# Revit family: РОСМА_Термоманометр
name_source: partatom
category: Арматура трубопроводов
revit_build: Autodesk Revit 2018 (Build: 20180423_1000(x64)
units: mm (PartAtom-declared; Revit-internal decimal feet)

## family parameters
Всегда вертикально = Да
На основе рабочей плоскости = Нет
Общий = Нет
При загрузке вырезать с полостями = Нет
Размер круглого соединителя = Использовать диаметр
Тип детали = Вставляется

## types (4) — shared parameters
ADSK_Единица измерения = шт.
ADSK_Количество = 1
DN = 15.00 мм
Table = спец_термоманометр
Table_2 = размеры_термоманометр
URL = https://rosma.spb.ru
Группа модели = Оборудование
Диапазон раб. температур изм. среды = от 0°С до +100°С
Длина01 = ᅠ : 46мм
Длина02 = ᅠ : 64мм
Длина03 = ᅠ : 100мм
Изготовитель = ЗАО "РОСМА"
Класс точности = 2,5
Климатическое исполнение = Группа В3 по ГОСТ Р 52931; климатическое исполнение УХЛ категории 3.1 по ГОСТ 15150
Код IP = IP40
Межповерочный интервал = 2 года
Температура01 = ‎ : (0...+120°С)(0...0.25МПа)
Температура02 = ‎ : (0...+120°С)(0...0.4МПа)
Температура03 = ‎ : (0...+120°С)(0...0.6МПа)
Температура04 = ‎ : (0...+120°С)(0...1.0МПа)
Температура05 = ‎ : (0...+120°С)(0...1.6МПа)
Температура06 = ‎ : (0...+120°С)(0...2.5МПа)
Температура07 = ‎ : (0...+150°С)(0...0.25МПа)
Температура08 = ‎ : (0...+150°С)(0...0.4МПа)
Температура09 = ‎ : (0...+150°С)(0...0.6МПа)
Температура10 = ‎ : (0...+150°С)(0...1.0МПа)
Температура11 = ‎ : (0...+150°С)(0...1.6МПа)
Температура12 = ‎ : (0...+150°С)(0...2.5МПа)
Техническая документация = ТУ 4212-001-4719015564-2008; ГОСТ 2405–88
лого_задн_стенка = Да

## per-type parameters (varying)
| type | Исполнение | Описание | Осевое присоединение | Радиальное присоединение |
| ТМТБ-31Р | 31 | Тип ТМТБ. Термоманометр радиальный — комбинированный прибор, предназначенный для измерения температуры и избыточного давления неагрессивных к медным сплавам сред в системах теплоснабжения и водоснабжения. | Нет | Да |
| ТМТБ-41Р | 41 | Тип ТМТБ. Термоманометр радиальный — комбинированный прибор, предназначенный для измерения температуры и избыточного давления неагрессивных к медным сплавам сред в системах теплоснабжения и водоснабжения. | Нет | Да |
| ТМТБ-31Т | 31 | Тип ТМТБ. Термоманометр осевой — комбинированный прибор, предназначенный для измерения температуры и избыточного давления неагрессивных к медным сплавам сред в системах теплоснабжения и водоснабжения. | Да | Нет |
| ТМТБ-41Т | 41 | Тип ТМТБ. Термоманометр осевой — комбинированный прибор, предназначенный для измерения температуры и избыточного давления неагрессивных к медным сплавам сред в системах теплоснабжения и водоснабжения. | Да | Нет |
